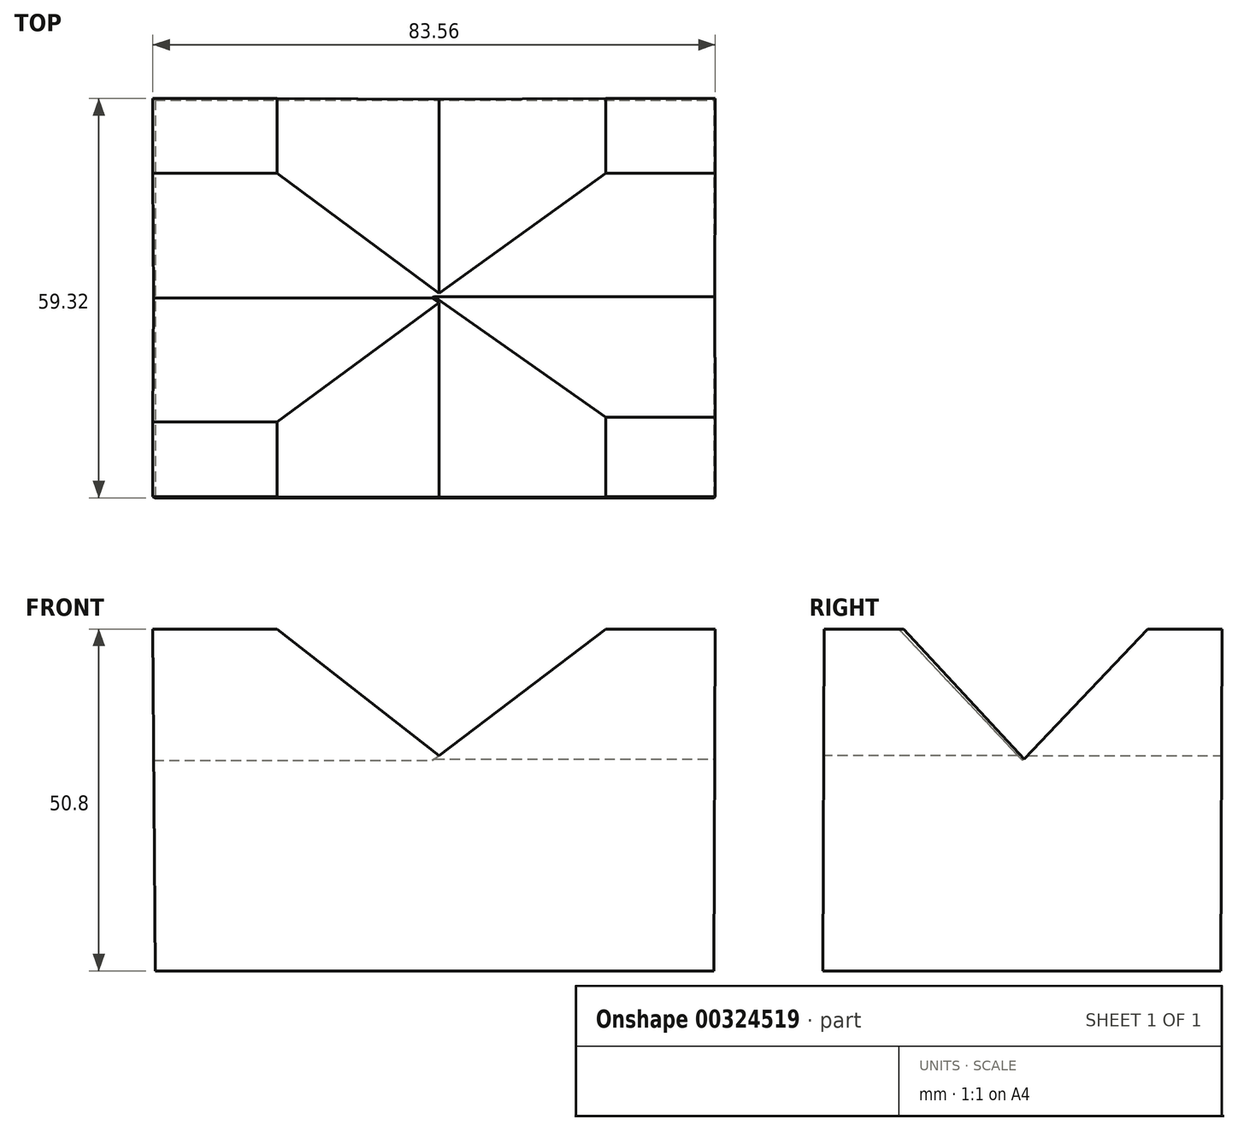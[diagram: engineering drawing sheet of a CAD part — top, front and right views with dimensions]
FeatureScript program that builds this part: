
annotation { "Feature Type Name" : "Feature", "Feature Type Description" : "" }
export const myFeature = defineFeature(function(context is Context, id is Id, definition is map)
    precondition{}
    {
        {
            var Q0;
            Q0=qCreatedBy(makeId("Top.planeOp"),FACE);
            var sketch = newSketch(context, id + "F0", { "sketchPlane" : qUnion([Q0])});
            skLineSegment(sketch, "E0.bottom", {"start": v(-29.55, 19.02) * mm, "end": v(53.44, 19.02) * mm});
            skLineSegment(sketch, "E0.top", {"start": v(-29.55, -40.08) * mm, "end": v(53.44, -40.08) * mm});
            skLineSegment(sketch, "E0.left", {"start": v(-29.55, 19.02) * mm, "end": v(-29.55, -40.08) * mm});
            skLineSegment(sketch, "E0.right", {"start": v(53.44, 19.02) * mm, "end": v(53.44, -40.08) * mm});
            skSolve(sketch);
        }
        {
            var Q0;
            Q0=qCreatedBy(makeId("Top.planeOp"),FACE);
            cPlane(context, id + "F1", {"entities" : qUnion([Q0]), "cplaneType" : CPlaneType.OFFSET, "offset" : 50.8 * mm, "width" : 152.4 * mm, "height" : 152.4 * mm});
        }
        {
            var Q0;
            Q0=qCreatedBy(id+"F1.planeOp",FACE);
            var sketch = newSketch(context, id + "F2", { "sketchPlane" : qUnion([Q0])});
            skLineSegment(sketch, "E1.bottom", {"start": v(-29.9, 19.24) * mm, "end": v(-11.41, 19.24) * mm});
            skLineSegment(sketch, "E1.top", {"start": v(-29.9, 8.15) * mm, "end": v(-11.41, 8.15) * mm});
            skLineSegment(sketch, "E1.left", {"start": v(-29.9, 19.24) * mm, "end": v(-29.9, 8.15) * mm});
            skLineSegment(sketch, "E1.right", {"start": v(-11.41, 19.24) * mm, "end": v(-11.41, 8.15) * mm});
            skLineSegment(sketch, "E2.bottom", {"start": v(-29.9, -39.92) * mm, "end": v(-11.41, -39.92) * mm});
            skLineSegment(sketch, "E2.top", {"start": v(-29.9, -28.83) * mm, "end": v(-11.41, -28.83) * mm});
            skLineSegment(sketch, "E2.left", {"start": v(-29.9, -39.92) * mm, "end": v(-29.9, -28.83) * mm});
            skLineSegment(sketch, "E2.right", {"start": v(-11.41, -39.92) * mm, "end": v(-11.41, -28.83) * mm});
            skLineSegment(sketch, "E3.bottom", {"start": v(53.66, -39.92) * mm, "end": v(37.4, -39.92) * mm});
            skLineSegment(sketch, "E3.top", {"start": v(53.66, -28.09) * mm, "end": v(37.4, -28.09) * mm});
            skLineSegment(sketch, "E3.left", {"start": v(53.66, -39.92) * mm, "end": v(53.66, -28.09) * mm});
            skLineSegment(sketch, "E3.right", {"start": v(37.4, -39.92) * mm, "end": v(37.4, -28.09) * mm});
            skLineSegment(sketch, "E4.bottom", {"start": v(53.66, 19.24) * mm, "end": v(37.4, 19.24) * mm});
            skLineSegment(sketch, "E4.top", {"start": v(53.66, 8.15) * mm, "end": v(37.4, 8.15) * mm});
            skLineSegment(sketch, "E4.left", {"start": v(53.66, 19.24) * mm, "end": v(53.66, 8.15) * mm});
            skLineSegment(sketch, "E4.right", {"start": v(37.4, 19.24) * mm, "end": v(37.4, 8.15) * mm});
            skSolve(sketch);
        }
        {
            var Q0;
            Q0=makeQuery(id+"F0.imprint","IMPRINT",FACE,{"disambiguationData":[TD([[makeQuery(id+"F0.imprint","IMPRINT",EDGE,{"derivedFrom":sQuery(id+"F0.wireOp",EDGE,"E0.bottom")}),-1.0]])]});
            var Q1;
            Q1=makeQuery(id+"F2.imprint","IMPRINT",FACE,{"disambiguationData":[TD([[makeQuery(id+"F2.imprint","IMPRINT",EDGE,{"derivedFrom":sQuery(id+"F2.wireOp",EDGE,"E1.bottom")}),-1.0]])]});
            loft(context, id + "F3", {"sheetProfilesArray" : [{ "sheetProfileEntities" : qUnion([Q0]) }, { "sheetProfileEntities" : qUnion([Q1]) }]});
        }
        {
            var Q1;
            Q1 = qSketchRegion(id + "F0", true);
            var Q2;
            Q2=makeQuery(id+"F2.imprint","IMPRINT",FACE,{"disambiguationData":[TD([[makeQuery(id+"F2.imprint","IMPRINT",EDGE,{"derivedFrom":sQuery(id+"F2.wireOp",EDGE,"E3.bottom")}),-1.0]])]});
            loft(context, id + "F4", {"operationType" : NewBodyOperationType.ADD, "sheetProfilesArray" : [{ "sheetProfileEntities" : qUnion([Q1]) }, { "sheetProfileEntities" : qUnion([Q2]) }]});
        }
        {
            var Q1;
            Q1=makeQuery(id+"F0.imprint","IMPRINT",FACE,{"disambiguationData":[TD([[makeQuery(id+"F0.imprint","IMPRINT",EDGE,{"derivedFrom":sQuery(id+"F0.wireOp",EDGE,"E0.bottom")}),-1.0]])]});
            var Q2;
            Q2=makeQuery(id+"F2.imprint","IMPRINT",FACE,{"disambiguationData":[TD([[makeQuery(id+"F2.imprint","IMPRINT",EDGE,{"derivedFrom":sQuery(id+"F2.wireOp",EDGE,"E2.bottom")}),1.0]])]});
            loft(context, id + "F5", {"operationType" : NewBodyOperationType.ADD, "sheetProfilesArray" : [{ "sheetProfileEntities" : qUnion([Q1]) }, { "sheetProfileEntities" : qUnion([Q2]) }]});
        }
        {
            var Q1;
            Q1=makeQuery(id+"F0.imprint","IMPRINT",FACE,{"disambiguationData":[TD([[makeQuery(id+"F0.imprint","IMPRINT",EDGE,{"derivedFrom":sQuery(id+"F0.wireOp",EDGE,"E0.bottom")}),-1.0]])]});
            var Q2;
            Q2=makeQuery(id+"F2.imprint","IMPRINT",FACE,{"disambiguationData":[TD([[makeQuery(id+"F2.imprint","IMPRINT",EDGE,{"derivedFrom":sQuery(id+"F2.wireOp",EDGE,"E4.bottom")}),1.0]])]});
            loft(context, id + "F6", {"operationType" : NewBodyOperationType.ADD, "sheetProfilesArray" : [{ "sheetProfileEntities" : qUnion([Q1]) }, { "sheetProfileEntities" : qUnion([Q2]) }]});
        }
    });
